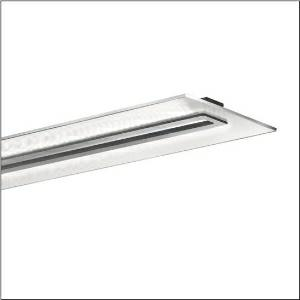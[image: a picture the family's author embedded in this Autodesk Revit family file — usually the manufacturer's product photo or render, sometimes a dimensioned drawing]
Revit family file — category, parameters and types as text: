
# Revit family: vega_r__11_5mn238dle0s_e1af
name_source: partatom
category: Lighting Fixtures
units: mm (PartAtom-declared; Revit-internal decimal feet)

## family parameters
Cut with Voids When Loaded = No
Host = Face
Light Source = No
Part Type = Normal
Room Calculation Point = No
Round Connector Dimension = Use Diameter
Shared = No

## types (1)
- --- (1 x LED 4000K / CRI = 80, 8130 lm, 62 W, 4000K)
    Apparent Load = 62 VA
    CIE Flux Codes = 61 86 97 62 100
    Color Rendering = 83
    Color Temperature = 4000K
    Default Elevation = 1800 mm
    Description = Vega® 11, office luminaire, primary light control with prismatic reflector, of PMMA, transparent prismatic structure, CAT 2 (L<= 1500cd/m²), light emission: direct/indirect distribution, primary light characteristic: symmetric, installation type: suspended mounting, surface-mounted, LED rated luminous flux: 8.130 lm, light colour: 840, colour temperature: 4000K, control gear: ECG, with terminal, 3+2-pole, max. 2.5mm², mains connection: 230V, AC, 50Hz, connection cable inclusive, cable length: 1,5 m, rated input power: 62W, luminaire housing, rectangular, rounded, of aluminium section, anodised, metallic grey (RAL 9006), length: 1.250 mm, width: 350 mm, height: 43mm, luminaire housing, lower part, of aluminium section, anodised, metallic grey (RAL 9006), of PC, grey, protection rating (complete): IP20, insulation class (complete): insulation class I (protective earthing), certification: CE, permissible ambient temperature for indoor applications: 0..+35°C, standard: EN 50419, packaging unit: 1 piece
    Height = 40 mm  [stored 0.131234 ft]
    Lamp = 1 x LED 4000K / CRI >= 80
    Lamp Light Flux = 8130 lm
    Lamp Power = 62 W
    Lamp count = 1
    Length = 1250 mm
    Luminous efficacy = 131 lm/W
    Manufacturer = Siteco
    ModVariant = No
    Model = 5MN238DLE0S
    Mounting Place = Ceiling
    Mounting Type = Pendant
    Number of Poles = 1
    OnlyDefault = Yes
    Power Factor = 1
    Product Name = Vega® 11
    Product group = office luminaire | ceiling pendant
    ProductGroupID = 905
    Protection Class = Protection class I
    Protection Degree = IP 20
    RLX_Detail_Level = 1
    RlxData = <blob elided: 63413 chars, md5=042a7842>
    Socket = socket
    Standby Power = 0 W
    System Light Flux = 8130 lm
    System Power = 62 W
    Type Comments = factory setting: luminous flux: 100 % | dim-lin: 254 | 458 mA
    Type Image = l_1004807.jpg
    URL = http://relux.com
    VarID = @adj_147289
    Voltage = 0 V
    Weight = 0.00 kg
    Width = 350 mm

note: [stored X ft] marks values corroborated as IEEE doubles in the binary element streams (Revit-internal decimal feet)

## geometry (parser evidence)
native form markers: Blend x4, Sweep x12
no freeform markers — native parametric forms only
